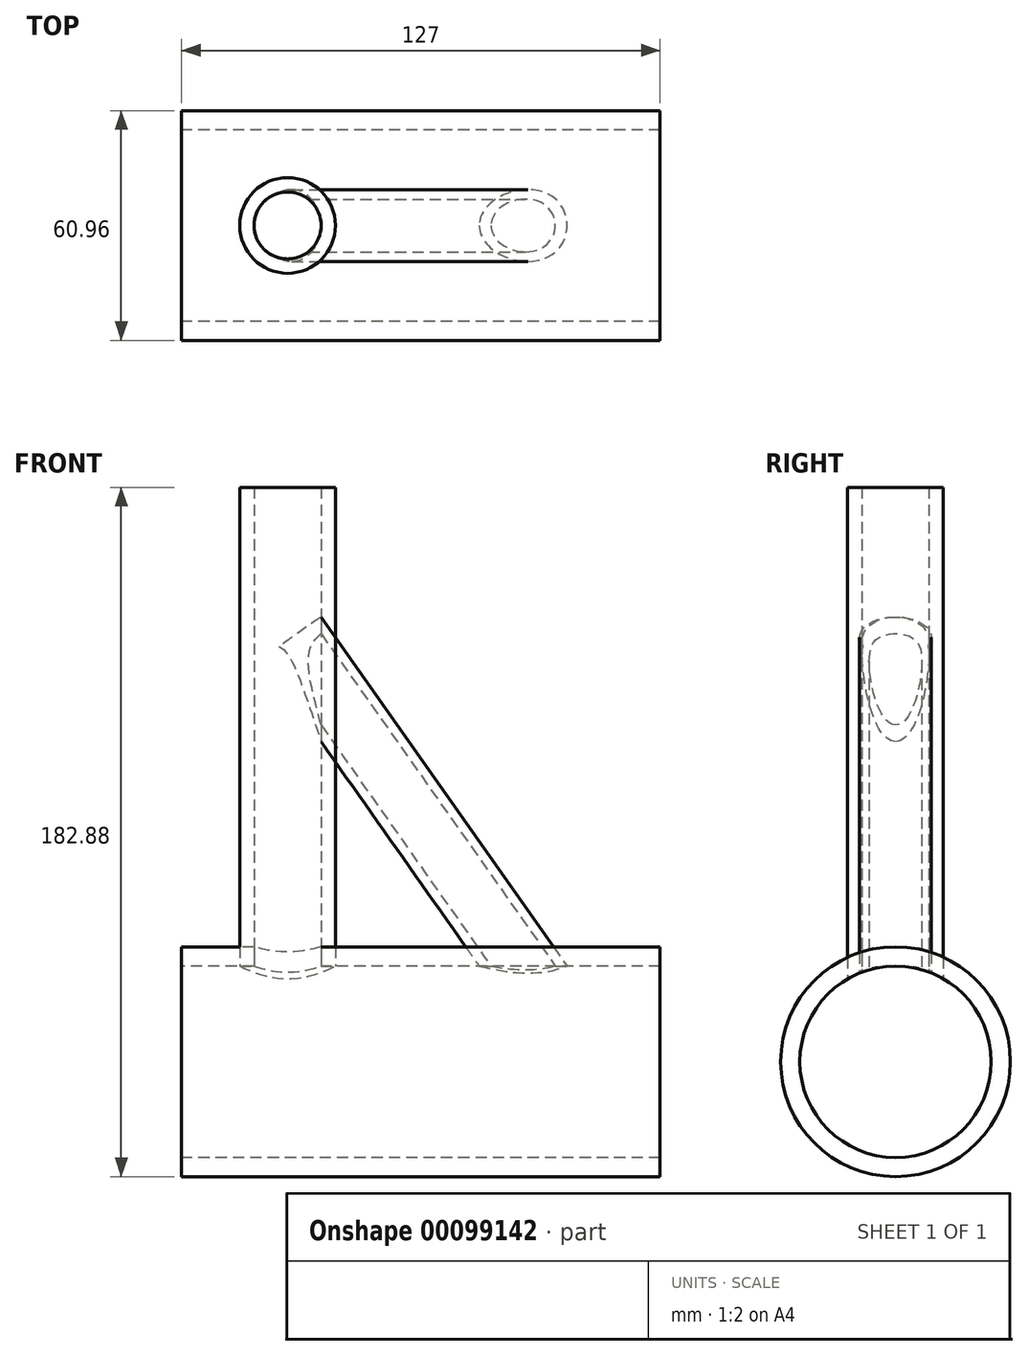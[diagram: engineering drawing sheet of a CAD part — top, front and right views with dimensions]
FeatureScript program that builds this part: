
annotation { "Feature Type Name" : "Feature", "Feature Type Description" : "" }
export const myFeature = defineFeature(function(context is Context, id is Id, definition is map)
    precondition{}
    {
        {
            var Q0;
            Q0=qCreatedBy(makeId("Right.planeOp"),FACE);
            var sketch = newSketch(context, id + "F0", { "sketchPlane" : qUnion([Q0])});
            skCircle(sketch, "E0", {"center": v(0, 0) * mm, "radius": 25.4 * mm});
            skCircle(sketch, "E1", {"center": v(0, 0) * mm, "radius": 30.48 * mm});
            skPoint(sketch, "E2", {"position": v(0, 30.48) * mm});
            skSolve(sketch);
        }
        {
            var Q0;
            Q0 = qSketchRegion(id + "F0", true);
            extrude(context, id + "F1", {"entities" : qUnion([Q0]), "endBound" : BoundingType.SYMMETRIC, "depth" : 127 * mm});
        }
        {
            var Q0;
            Q0=qCreatedBy(makeId("Top.planeOp"),FACE);
            var sketch = newSketch(context, id + "F2", { "sketchPlane" : qUnion([Q0])});
            skCircle(sketch, "E3", {"center": v(-35.38, 0) * mm, "radius": 8.9 * mm});
            skCircle(sketch, "E4", {"center": v(-35.38, 0) * mm, "radius": 12.7 * mm});
            skSolve(sketch);
        }
        {
            var Q0;
            Q0=makeQuery(id+"F2.imprint","IMPRINT",FACE,{"disambiguationData":[TD([[makeQuery(id+"F2.imprint","IMPRINT",EDGE,{"derivedFrom":sQuery(id+"F2.wireOp",EDGE,"E3")}),-1.0]])]});
            extrude(context, id + "F3", {"entities" : qUnion([Q0]), "depth" : 152.4 * mm});
        }
        {
            var Q0;
            Q0=makeQuery(id+"F2.imprint","IMPRINT",FACE,{"disambiguationData":[TD([[makeQuery(id+"F2.imprint","IMPRINT",EDGE,{"derivedFrom":sQuery(id+"F2.wireOp",EDGE,"E3")}),1.0]])]});
            extrude(context, id + "F4", {"entities" : qUnion([Q0]), "operationType" : NewBodyOperationType.REMOVE, "depth" : 127 * mm});
        }
        {
            var Q0;
            Q0=qCreatedBy(makeId("Front.planeOp"),FACE);
            var sketch = newSketch(context, id + "F5", { "sketchPlane" : qUnion([Q0])});
            skLineSegment(sketch, "E5", {"start": v(19.8, 10.84) * mm, "end": v(52.56, 33.93) * mm, "construction": true});
            skSolve(sketch);
        }
        {
            var Q0;
            Q0=sQuery(id+"F5.wireOp",EDGE,"E5");
            cPlane(context, id + "F6", {"entities" : qUnion([Q0]), "cplaneType" : CPlaneType.LINE_ANGLE, "offset" : 152.4 * mm, "angle" : 90 * degree, "width" : 152.4 * mm, "height" : 152.4 * mm});
        }
        {
            var Q0;
            Q0=qCreatedBy(id+"F6.planeOp",FACE);
            var sketch = newSketch(context, id + "F7", { "sketchPlane" : qUnion([Q0])});
            skCircle(sketch, "E6", {"center": v(36.8, 0) * mm, "radius": 9.53 * mm});
            skCircle(sketch, "E7", {"center": v(36.8, 0) * mm, "radius": 6.99 * mm});
            skSolve(sketch);
        }
        {
            var Q0;
            Q0=makeQuery(id+"F7.imprint","IMPRINT",FACE,{"disambiguationData":[TD([[makeQuery(id+"F7.imprint","IMPRINT",EDGE,{"derivedFrom":sQuery(id+"F7.wireOp",EDGE,"E6")}),1.0]])]});
            var Q1;
            Q1=sQuery(id+"F7.wireOp",EDGE,"E6");
            var Q2;
            Q2=sQuery(id+"F7.wireOp",EDGE,"E7");
            extrude(context, id + "F8", {"entities" : qUnion([Q0]), "surfaceEntities" : qUnion([Q1, Q2]), "depth" : 114.3 * mm});
        }
        {
            var Q0;
            Q0=makeQuery(id+"F0.imprint","IMPRINT",FACE,{"disambiguationData":[TD([[makeQuery(id+"F0.imprint","IMPRINT",EDGE,{"derivedFrom":sQuery(id+"F0.wireOp",EDGE,"E0")}),1.0]])]});
            extrude(context, id + "F9", {"entities" : qUnion([Q0]), "operationType" : NewBodyOperationType.REMOVE, "endBound" : BoundingType.SYMMETRIC, "oppositeDirection" : true, "depth" : 127 * mm});
        }
        {
            var Q0;
            Q0=makeQuery(id+"F2.imprint","IMPRINT",FACE,{"disambiguationData":[TD([[makeQuery(id+"F2.imprint","IMPRINT",EDGE,{"derivedFrom":sQuery(id+"F2.wireOp",EDGE,"E3")}),1.0]])]});
            extrude(context, id + "F10", {"entities" : qUnion([Q0]), "operationType" : NewBodyOperationType.REMOVE, "depth" : 152.4 * mm});
        }
    });
